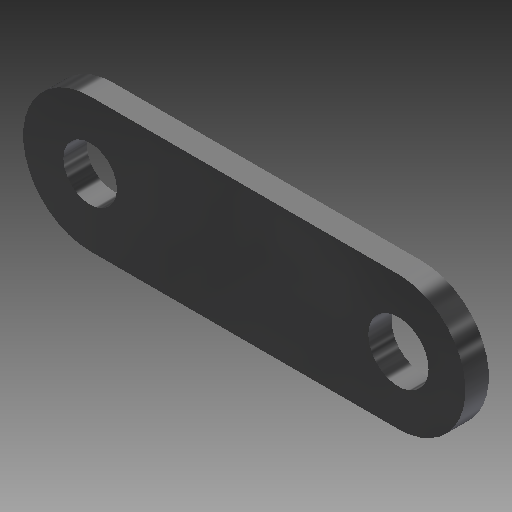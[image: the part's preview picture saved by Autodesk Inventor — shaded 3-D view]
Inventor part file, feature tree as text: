
AUTODESK INVENTOR PART (.ipt)
format: ipt  version: 2019 (Build 230136000, 136)  size: 107,008 bytes
history: native  units: mm
features: hole x2, extrude x1, sketch x1
ambient origin geometry x8: Origin, YZ Plane, XZ Plane, XY Plane, X Axis, Y Axis, Z Axis, Center Point
bodies: Solid1 (feature_tree)
feature tree (4):
  extrude  "Extrusion1"  Depth=20.0mm
  hole  "Hole3"  [1 undecoded]
  hole  "Hole4"  [1 undecoded]
  sketch  "Sketch1"  dims[d0=20.0mm d1=20.0mm d2=46.0mm d3=3.5mm d4=0.0mm d19=10.0mm d20=10.0mm d21=8.0mm d22=6.0mm d23=4.0mm d24=2.0mm d25=90.0deg d26=8.0mm d27=20.594885mm d28=10.0mm d29=10.0mm d30=9.0mm d31=6.0mm d32=4.0mm d33=2.0mm d34=90.0deg d35=8.0mm d36=20.594885mm d37=1.0mm d38=1.0mm]
note: 2 required parameter values undecoded (feature->parameter linkage not recoverable at this tier; creation-order binding heuristic only, values carry confidence <= 0.55)
